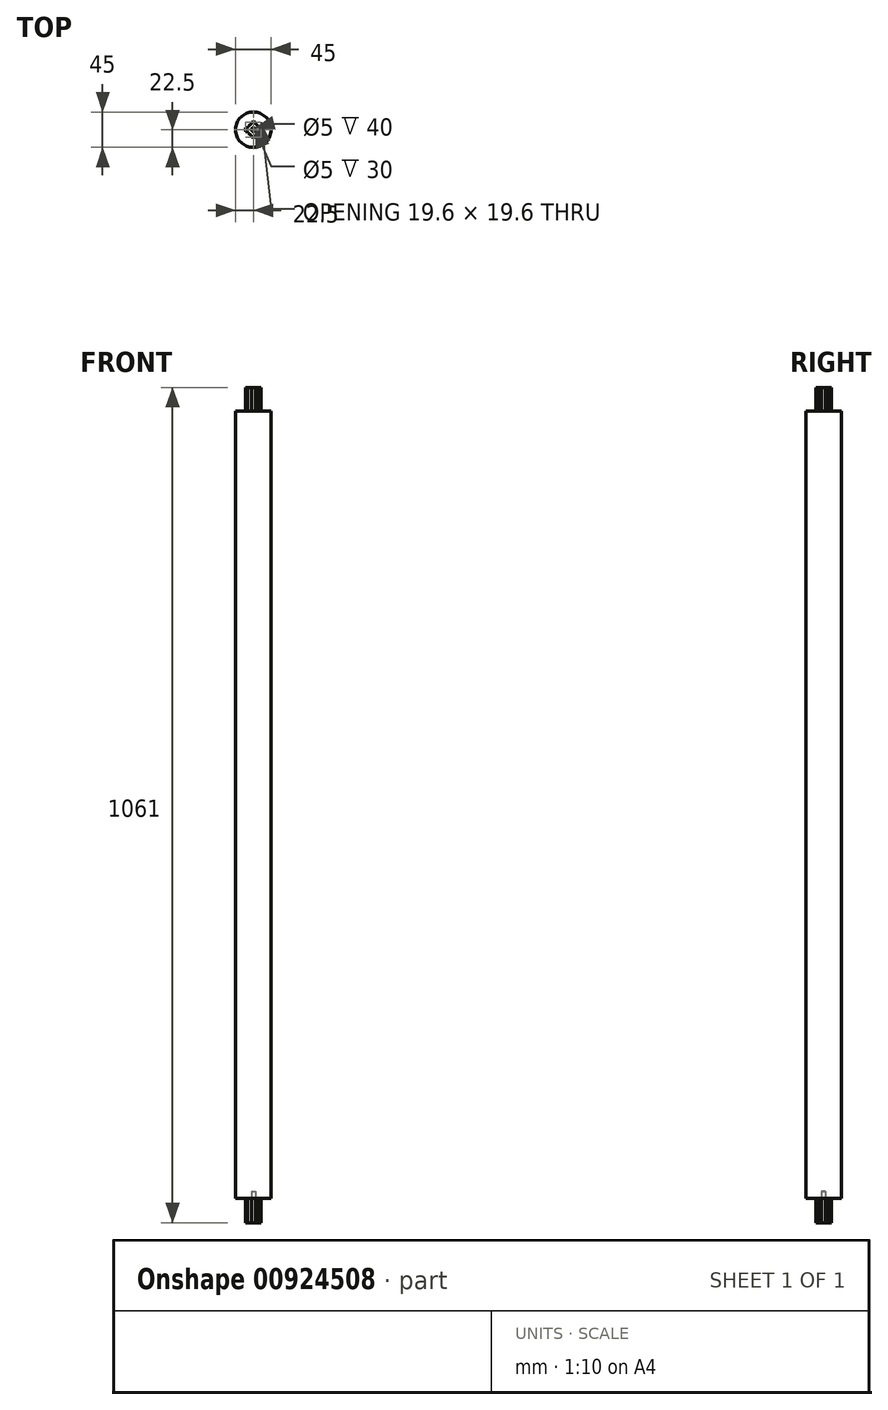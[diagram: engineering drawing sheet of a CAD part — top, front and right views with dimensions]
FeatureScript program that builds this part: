
annotation { "Feature Type Name" : "Feature", "Feature Type Description" : "" }
export const myFeature = defineFeature(function(context is Context, id is Id, definition is map)
    precondition{}
    {
        {
            var Q0;
            Q0=qCreatedBy(makeId("Top.planeOp"),FACE);
            var sketch = newSketch(context, id + "F0", { "sketchPlane" : qUnion([Q0])});
            skCircle(sketch, "E0", {"center": v(0, 0) * mm, "radius": 22.5 * mm});
            skSolve(sketch);
        }
        {
            var Q0;
            Q0=makeQuery(id+"F0.imprint","IMPRINT",FACE,{"disambiguationData":[TD([[makeQuery(id+"F0.imprint","IMPRINT",EDGE,{"derivedFrom":sQuery(id+"F0.wireOp",EDGE,"E0")}),1.0]])]});
            extrude(context, id + "F1", {"entities" : qUnion([Q0]), "depth" : 1000 * mm, "offsetDistance" : 25 * mm});
        }
        {
            var Q0;
            Q0=makeQuery(id+"F1.opExtrude","CAP_FACE",FACE,{"disambiguationData":[OSD([sQuery(id+"F0.wireOp",EDGE,"E0")])],"isStart":false});
            var sketch = newSketch(context, id + "F2", { "sketchPlane" : qUnion([Q0])});
            skCircle(sketch, "E1", {"center": v(0, 0) * mm, "radius": 7.5 * mm});
            skLineSegment(sketch, "E2", {"start": v(0, 9.8) * mm, "end": v(-2.5, 9.8) * mm});
            skLineSegment(sketch, "E3", {"start": v(0, 9.8) * mm, "end": v(2.5, 9.8) * mm});
            skLineSegment(sketch, "E4", {"start": v(2.5, 9.8) * mm, "end": v(2.5, 7.07) * mm});
            skLineSegment(sketch, "E5", {"start": v(-2.5, 9.8) * mm, "end": v(-2.5, 7.07) * mm});
            skLineSegment(sketch, "E6.1.0", {"start": v(-9.8, 0) * mm, "end": v(-9.8, 2.5) * mm});
            skLineSegment(sketch, "E6.1.1", {"start": v(-9.8, 2.5) * mm, "end": v(-7.07, 2.5) * mm});
            skLineSegment(sketch, "E6.1.2", {"start": v(-9.8, 0) * mm, "end": v(-9.8, -2.5) * mm});
            skLineSegment(sketch, "E6.1.3", {"start": v(-9.8, -2.5) * mm, "end": v(-7.07, -2.5) * mm});
            skLineSegment(sketch, "E6.2.0", {"start": v(0, -9.8) * mm, "end": v(-2.5, -9.8) * mm});
            skLineSegment(sketch, "E6.2.1", {"start": v(-2.5, -9.8) * mm, "end": v(-2.5, -7.07) * mm});
            skLineSegment(sketch, "E6.2.2", {"start": v(0, -9.8) * mm, "end": v(2.5, -9.8) * mm});
            skLineSegment(sketch, "E6.2.3", {"start": v(2.5, -9.8) * mm, "end": v(2.5, -7.07) * mm});
            skLineSegment(sketch, "E6.3.0", {"start": v(9.8, 0) * mm, "end": v(9.8, -2.5) * mm});
            skLineSegment(sketch, "E6.3.1", {"start": v(9.8, -2.5) * mm, "end": v(7.07, -2.5) * mm});
            skLineSegment(sketch, "E6.3.2", {"start": v(9.8, 0) * mm, "end": v(9.8, 2.5) * mm});
            skLineSegment(sketch, "E6.3.3", {"start": v(9.8, 2.5) * mm, "end": v(7.07, 2.5) * mm});
            skSolve(sketch);
        }
        {
            var Q0;
            Q0=makeQuery(id+"F1.opExtrude","CAP_FACE",FACE,{"disambiguationData":[OSD([sQuery(id+"F0.wireOp",EDGE,"E0")])],"isStart":true});
            var sketch = newSketch(context, id + "F3", { "sketchPlane" : qUnion([Q0])});
            skCircle(sketch, "E7", {"center": v(0, 0) * mm, "radius": 7.5 * mm});
            skLineSegment(sketch, "E8", {"start": v(0, 9.8) * mm, "end": v(-2.5, 9.8) * mm});
            skLineSegment(sketch, "E9", {"start": v(0, 9.8) * mm, "end": v(2.5, 9.8) * mm});
            skLineSegment(sketch, "E10", {"start": v(2.5, 9.8) * mm, "end": v(2.5, 7.07) * mm});
            skLineSegment(sketch, "E11", {"start": v(-2.5, 9.8) * mm, "end": v(-2.5, 7.07) * mm});
            skLineSegment(sketch, "E12.1.0", {"start": v(-9.8, 0) * mm, "end": v(-9.8, 2.5) * mm});
            skLineSegment(sketch, "E12.1.1", {"start": v(-9.8, 2.5) * mm, "end": v(-7.07, 2.5) * mm});
            skLineSegment(sketch, "E12.1.2", {"start": v(-9.8, 0) * mm, "end": v(-9.8, -2.5) * mm});
            skLineSegment(sketch, "E12.1.3", {"start": v(-9.8, -2.5) * mm, "end": v(-7.07, -2.5) * mm});
            skLineSegment(sketch, "E12.2.0", {"start": v(0, -9.8) * mm, "end": v(-2.5, -9.8) * mm});
            skLineSegment(sketch, "E12.2.1", {"start": v(-2.5, -9.8) * mm, "end": v(-2.5, -7.07) * mm});
            skLineSegment(sketch, "E12.2.2", {"start": v(0, -9.8) * mm, "end": v(2.5, -9.8) * mm});
            skLineSegment(sketch, "E12.2.3", {"start": v(2.5, -9.8) * mm, "end": v(2.5, -7.07) * mm});
            skLineSegment(sketch, "E12.3.0", {"start": v(9.8, 0) * mm, "end": v(9.8, -2.5) * mm});
            skLineSegment(sketch, "E12.3.1", {"start": v(9.8, -2.5) * mm, "end": v(7.07, -2.5) * mm});
            skLineSegment(sketch, "E12.3.2", {"start": v(9.8, 0) * mm, "end": v(9.8, 2.5) * mm});
            skLineSegment(sketch, "E12.3.3", {"start": v(9.8, 2.5) * mm, "end": v(7.07, 2.5) * mm});
            skSolve(sketch);
        }
        {
            var Q0;
            Q0=makeQuery(id+"F3.imprint","IMPRINT",FACE,{"disambiguationData":[TD([[makeQuery(id+"F3.imprint","IMPRINT",EDGE,{"derivedFrom":sQuery(id+"F3.wireOp",EDGE,"E12.3.0")}),-1.0]])]});
            var Q1;
            Q1=makeQuery(id+"F3.imprint","IMPRINT",FACE,{"disambiguationData":[TD([[makeQuery(id+"F3.imprint","IMPRINT",EDGE,{"derivedFrom":sQuery(id+"F3.wireOp",EDGE,"E12.2.0")}),-1.0]])]});
            var Q2;
            Q2=makeQuery(id+"F3.imprint","IMPRINT",FACE,{"disambiguationData":[TD([[makeQuery(id+"F3.imprint","IMPRINT",EDGE,{"derivedFrom":sQuery(id+"F3.wireOp",EDGE,"E12.1.0")}),-1.0]])]});
            var Q3;
            {var subQ0=sQuery(id+"F3.wireOp",EDGE,"E7");var subQ4=makeQuery(id+"F3.imprint","INTERSECT",VERTEX,{"derivedFrom":[subQ0,sQuery(id+"F3.wireOp",EDGE,"E10")]});Q3=makeQuery(id+"F3.imprint","IMPRINT",FACE,{"disambiguationData":[TD([[makeQuery(id+"F3.imprint","IMPRINT",EDGE,{"disambiguationData":[TD([[subQ4,1.0]])],"derivedFrom":subQ0}),1.0]])]});}
            var Q4;
            Q4=makeQuery(id+"F3.imprint","IMPRINT",FACE,{"disambiguationData":[TD([[makeQuery(id+"F3.imprint","IMPRINT",EDGE,{"derivedFrom":sQuery(id+"F3.wireOp",EDGE,"E8")}),1.0]])]});
            extrude(context, id + "F4", {"entities" : qUnion([Q0, Q1, Q2, Q3, Q4]), "operationType" : NewBodyOperationType.ADD, "depth" : 31 * mm, "offsetDistance" : 25 * mm});
        }
        {
            var Q0;
            Q0=makeQuery(id+"F4.opExtrude","CAP_FACE",FACE,{"disambiguationData":[OSD([sQuery(id+"F3.wireOp",EDGE,"E7"),sQuery(id+"F3.wireOp",EDGE,"E8"),sQuery(id+"F3.wireOp",EDGE,"E9"),sQuery(id+"F3.wireOp",EDGE,"E10"),sQuery(id+"F3.wireOp",EDGE,"E11"),sQuery(id+"F3.wireOp",EDGE,"E12.1.0"),sQuery(id+"F3.wireOp",EDGE,"E12.1.1"),sQuery(id+"F3.wireOp",EDGE,"E12.1.2"),sQuery(id+"F3.wireOp",EDGE,"E12.1.3"),sQuery(id+"F3.wireOp",EDGE,"E12.2.0"),sQuery(id+"F3.wireOp",EDGE,"E12.2.1"),sQuery(id+"F3.wireOp",EDGE,"E12.2.2"),sQuery(id+"F3.wireOp",EDGE,"E12.2.3"),sQuery(id+"F3.wireOp",EDGE,"E12.3.0"),sQuery(id+"F3.wireOp",EDGE,"E12.3.1"),sQuery(id+"F3.wireOp",EDGE,"E12.3.2"),sQuery(id+"F3.wireOp",EDGE,"E12.3.3")])],"isStart":false});
            var sketch = newSketch(context, id + "F5", { "sketchPlane" : qUnion([Q0])});
            skCircle(sketch, "E13", {"center": v(0, 0) * mm, "radius": 2.5 * mm});
            skSolve(sketch);
        }
        {
            var Q0;
            Q0=qSketchRegion(id+"F5",true);
            extrude(context, id + "F6", {"entities" : qUnion([Q0]), "operationType" : NewBodyOperationType.REMOVE, "oppositeDirection" : true, "depth" : 40 * mm, "offsetDistance" : 25 * mm});
        }
        {
            var Q0;
            {var subQ0=sQuery(id+"F2.wireOp",EDGE,"E1");var subQ4=makeQuery(id+"F2.imprint","INTERSECT",VERTEX,{"derivedFrom":[subQ0,sQuery(id+"F2.wireOp",EDGE,"E4")]});Q0=makeQuery(id+"F2.imprint","IMPRINT",FACE,{"disambiguationData":[TD([[makeQuery(id+"F2.imprint","IMPRINT",EDGE,{"disambiguationData":[TD([[subQ4,1.0]])],"derivedFrom":subQ0}),1.0]])]});}
            var Q1;
            Q1=makeQuery(id+"F2.imprint","IMPRINT",FACE,{"disambiguationData":[TD([[makeQuery(id+"F2.imprint","IMPRINT",EDGE,{"derivedFrom":sQuery(id+"F2.wireOp",EDGE,"E6.1.0")}),-1.0]])]});
            var Q2;
            Q2=makeQuery(id+"F2.imprint","IMPRINT",FACE,{"disambiguationData":[TD([[makeQuery(id+"F2.imprint","IMPRINT",EDGE,{"derivedFrom":sQuery(id+"F2.wireOp",EDGE,"E2")}),1.0]])]});
            var Q3;
            Q3=makeQuery(id+"F2.imprint","IMPRINT",FACE,{"disambiguationData":[TD([[makeQuery(id+"F2.imprint","IMPRINT",EDGE,{"derivedFrom":sQuery(id+"F2.wireOp",EDGE,"E6.3.0")}),-1.0]])]});
            var Q4;
            Q4=makeQuery(id+"F2.imprint","IMPRINT",FACE,{"disambiguationData":[TD([[makeQuery(id+"F2.imprint","IMPRINT",EDGE,{"derivedFrom":sQuery(id+"F2.wireOp",EDGE,"E6.2.0")}),-1.0]])]});
            extrude(context, id + "F7", {"entities" : qUnion([Q0, Q1, Q2, Q3, Q4]), "operationType" : NewBodyOperationType.ADD, "depth" : 30 * mm, "offsetDistance" : 25 * mm});
        }
        {
            var Q0;
            Q0=makeQuery(id+"F7.opExtrude","CAP_FACE",FACE,{"disambiguationData":[OSD([sQuery(id+"F2.wireOp",EDGE,"E1"),sQuery(id+"F2.wireOp",EDGE,"E2"),sQuery(id+"F2.wireOp",EDGE,"E3"),sQuery(id+"F2.wireOp",EDGE,"E4"),sQuery(id+"F2.wireOp",EDGE,"E5"),sQuery(id+"F2.wireOp",EDGE,"E6.1.0"),sQuery(id+"F2.wireOp",EDGE,"E6.1.1"),sQuery(id+"F2.wireOp",EDGE,"E6.1.2"),sQuery(id+"F2.wireOp",EDGE,"E6.1.3"),sQuery(id+"F2.wireOp",EDGE,"E6.2.0"),sQuery(id+"F2.wireOp",EDGE,"E6.2.1"),sQuery(id+"F2.wireOp",EDGE,"E6.2.2"),sQuery(id+"F2.wireOp",EDGE,"E6.2.3"),sQuery(id+"F2.wireOp",EDGE,"E6.3.0"),sQuery(id+"F2.wireOp",EDGE,"E6.3.1"),sQuery(id+"F2.wireOp",EDGE,"E6.3.2"),sQuery(id+"F2.wireOp",EDGE,"E6.3.3")])],"isStart":false});
            var sketch = newSketch(context, id + "F8", { "sketchPlane" : qUnion([Q0])});
            skCircle(sketch, "E14", {"center": v(0, 0) * mm, "radius": 2.5 * mm});
            skSolve(sketch);
        }
        {
            var Q0;
            Q0=qSketchRegion(id+"F8",true);
            extrude(context, id + "F9", {"entities" : qUnion([Q0]), "operationType" : NewBodyOperationType.REMOVE, "oppositeDirection" : true, "depth" : 30 * mm, "offsetDistance" : 25 * mm});
        }
    });
